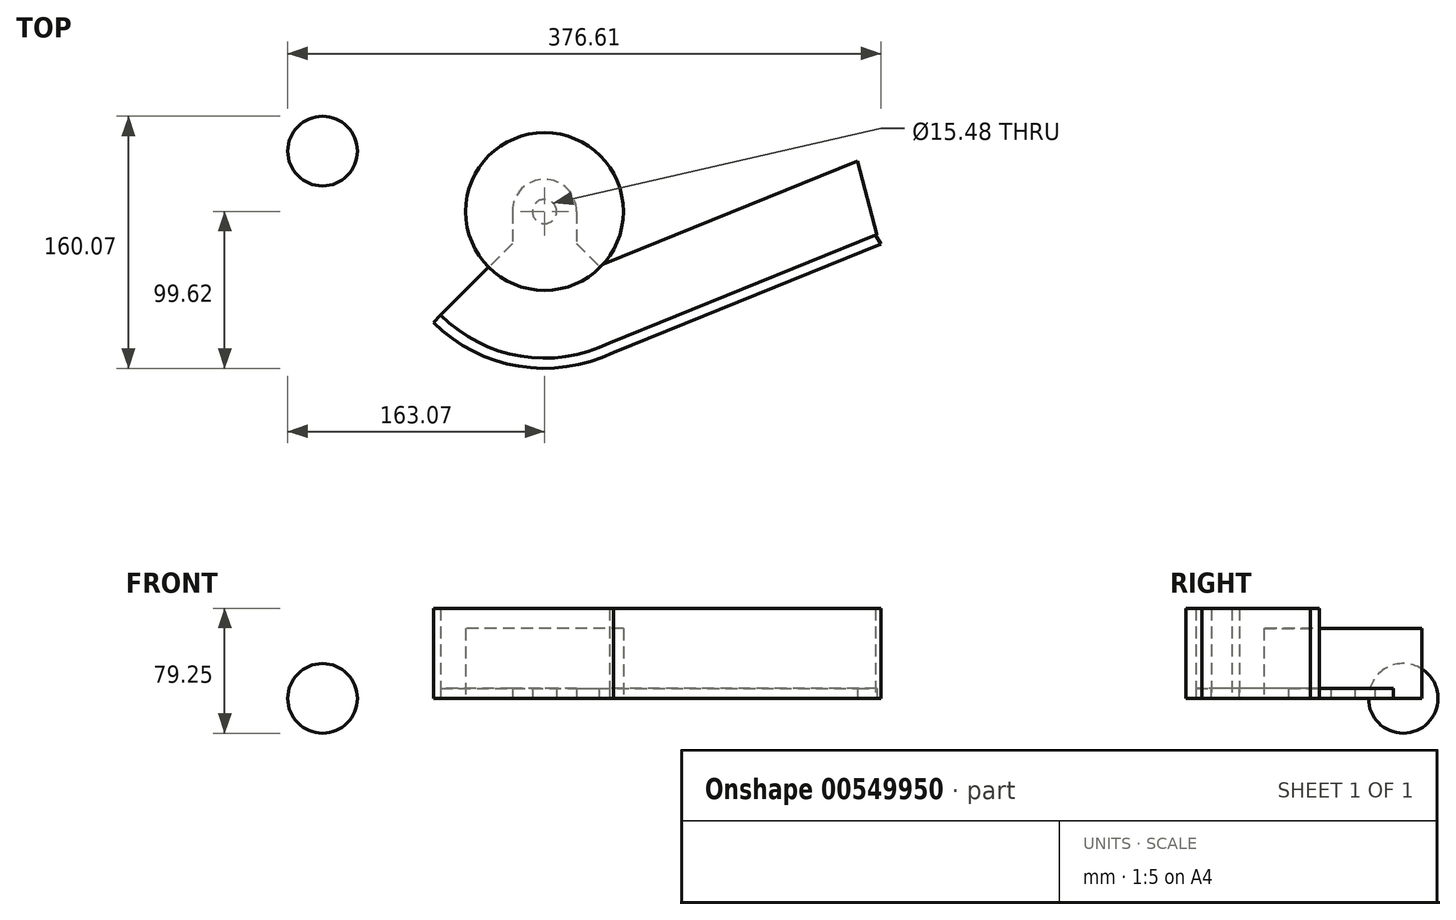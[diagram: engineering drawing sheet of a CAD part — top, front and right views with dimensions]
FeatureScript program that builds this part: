
annotation { "Feature Type Name" : "Feature", "Feature Type Description" : "" }
export const myFeature = defineFeature(function(context is Context, id is Id, definition is map)
    precondition{}
    {
        {
            var Q0;
            Q0=qCreatedBy(makeId("Top.planeOp"),FACE);
            var sketch = newSketch(context, id + "F0", { "sketchPlane" : qUnion([Q0])});
            skCircle(sketch, "E0", {"center": v(0, 0) * mm, "radius": 50.09 * mm});
            skSolve(sketch);
        }
        {
            var Q0;
            Q0 = qSketchRegion(id + "F0", true);
            extrude(context, id + "F1", {"entities" : qUnion([Q0]), "depth" : 44.45 * mm, "offsetDistance" : 25.4 * mm});
        }
        {
            var Q0;
            Q0=qCreatedBy(makeId("Top.planeOp"),FACE);
            var sketch = newSketch(context, id + "F2", { "sketchPlane" : qUnion([Q0])});
            skArc(sketch, "E1.0", {"start": v(-65.95, -65.95) * mm, "mid": v(-15.2, -92.02) * mm, "end": v(41.23, -83.66) * mm});
            skLineSegment(sketch, "E2", {"start": v(-20.45, -20.45) * mm, "end": v(-65.95, -65.95) * mm});
            skArc(sketch, "E3", {"start": v(-20.45, 0) * mm, "mid": v(0, 20.45) * mm, "end": v(20.45, 0) * mm});
            skLineSegment(sketch, "E4", {"start": v(-20.45, 0) * mm, "end": v(-20.45, -20.45) * mm});
            skLineSegment(sketch, "E5", {"start": v(20.45, -20.45) * mm, "end": v(34.52, -34.52) * mm});
            skLineSegment(sketch, "E6", {"start": v(20.45, 0) * mm, "end": v(20.45, -20.45) * mm});
            skCircle(sketch, "E7", {"center": v(0, 0) * mm, "radius": 7.74 * mm});
            skLineSegment(sketch, "E8", {"start": v(34.52, -34.52) * mm, "end": v(198.69, 31.99) * mm});
            skLineSegment(sketch, "E9", {"start": v(211.16, -14.82) * mm, "end": v(41.23, -83.66) * mm});
            skLineSegment(sketch, "E10", {"start": v(198.69, 31.99) * mm, "end": v(211.16, -14.82) * mm});
            skSolve(sketch);
        }
        {
            var Q0;
            Q0 = qSketchRegion(id + "F2", true);
            extrude(context, id + "F3", {"entities" : qUnion([Q0]), "depth" : 6.35 * mm, "offsetDistance" : 25.4 * mm});
        }
        {
            var Q0;
            Q0=qCreatedBy(makeId("Top.planeOp"),FACE);
            var sketch = newSketch(context, id + "F4", { "sketchPlane" : qUnion([Q0])});
            skLineSegment(sketch, "E11.0", {"start": v(213.54, -20.7) * mm, "end": v(43.82, -89.46) * mm});
            skArc(sketch, "E11.1", {"start": v(-70.44, -70.44) * mm, "mid": v(-16.36, -98.27) * mm, "end": v(43.82, -89.46) * mm});
            skLineSegment(sketch, "E12", {"start": v(-70.44, -70.44) * mm, "end": v(-66, -65.79) * mm});
            skArc(sketch, "E13", {"start": v(-66, -65.79) * mm, "mid": v(-15.17, -91.95) * mm, "end": v(41.38, -83.5) * mm});
            skLineSegment(sketch, "E14", {"start": v(41.38, -83.5) * mm, "end": v(210.33, -15.05) * mm});
            skLineSegment(sketch, "E15", {"start": v(210.33, -15.05) * mm, "end": v(213.54, -20.7) * mm});
            skSolve(sketch);
        }
        {
            var Q0;
            Q0 = qSketchRegion(id + "F4", true);
            extrude(context, id + "F5", {"entities" : qUnion([Q0]), "depth" : 57.15 * mm, "offsetDistance" : 25.4 * mm});
        }
        {
            var Q0;
            Q0=qCreatedBy(makeId("Top.planeOp"),FACE);
            var sketch = newSketch(context, id + "F6", { "sketchPlane" : qUnion([Q0])});
            skArc(sketch, "E16", {"start": v(-140.97, 60.45) * mm, "mid": v(-163.07, 38.35) * mm, "end": v(-140.97, 16.26) * mm});
            skLineSegment(sketch, "E17", {"start": v(-140.97, 38.35) * mm, "end": v(-140.97, 60.45) * mm, "construction": true});
            skLineSegment(sketch, "E18", {"start": v(-140.97, 38.35) * mm, "end": v(-140.97, -28.47) * mm});
            skLineSegment(sketch, "E19", {"start": v(-140.97, 16.26) * mm, "end": v(-140.97, 60.45) * mm});
            skSolve(sketch);
        }
        {
            var Q0;
            Q0=makeQuery(id+"F6.imprint","IMPRINT",FACE,{"disambiguationData":[TD([[makeQuery(id+"F6.imprint","IMPRINT",EDGE,{"derivedFrom":sQuery(id+"F6.wireOp",EDGE,"E16")}),1.0]])]});
            var Q1;
            Q1=sQuery(id+"F6.wireOp",EDGE,"E17");
            revolve(context, id + "F7", {"entities" : qUnion([Q0]), "axis" : qUnion([Q1]), "revolveType" : RevolveType.FULL});
        }
    });
